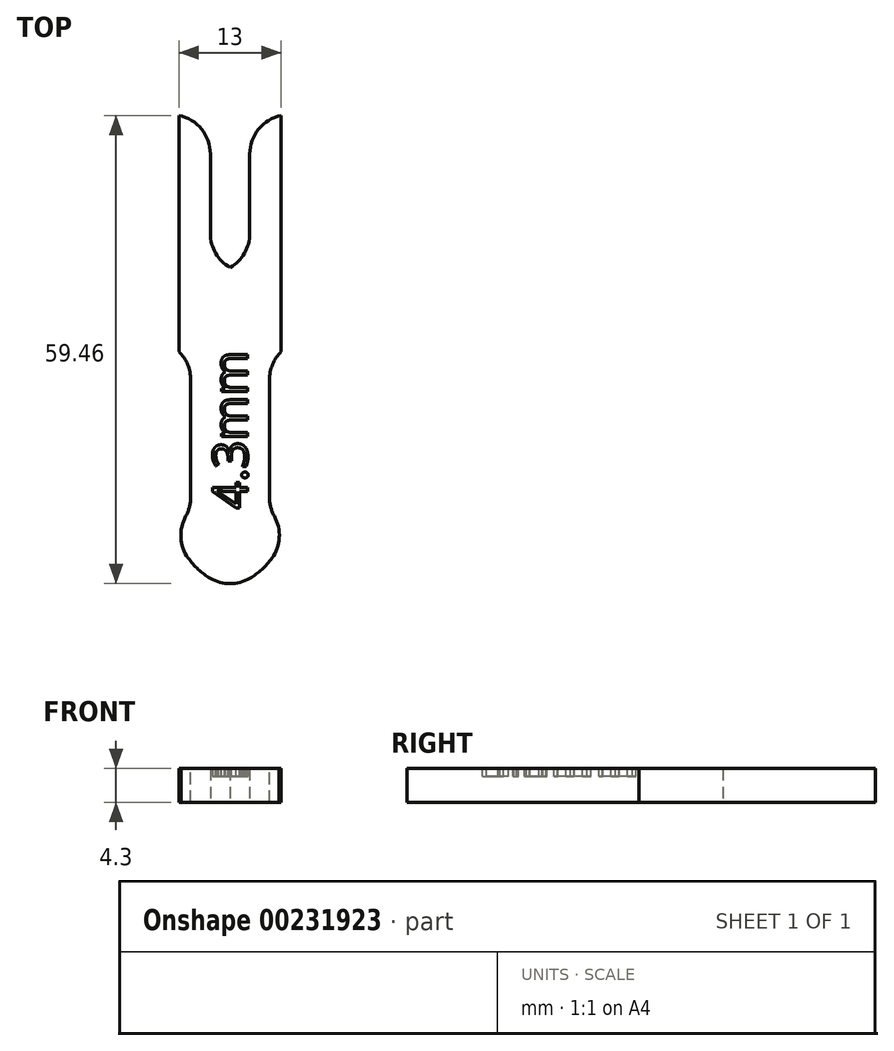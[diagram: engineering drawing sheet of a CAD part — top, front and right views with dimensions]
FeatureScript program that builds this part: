
annotation { "Feature Type Name" : "Feature", "Feature Type Description" : "" }
export const myFeature = defineFeature(function(context is Context, id is Id, definition is map)
    precondition{}
    {
        {
            var Q0;
            Q0=qCreatedBy(makeId("Top.planeOp"),FACE);
            var sketch = newSketch(context, id + "F0", { "sketchPlane" : qUnion([Q0])});
            skLineSegment(sketch, "E0", {"start": v(0, 0) * mm, "end": v(7, 0) * mm});
            skLineSegment(sketch, "E1", {"start": v(7, 0) * mm, "end": v(7, 10) * mm});
            skLineSegment(sketch, "E2", {"start": v(7, 10) * mm, "end": v(5, 10) * mm});
            skLineSegment(sketch, "E3", {"start": v(5, 10) * mm, "end": v(5, 30) * mm});
            skLineSegment(sketch, "E4", {"start": v(5, 30) * mm, "end": v(6.5, 30) * mm});
            skLineSegment(sketch, "E5", {"start": v(6.5, 30) * mm, "end": v(6.5, 60) * mm});
            skLineSegment(sketch, "E6", {"start": v(6.5, 60) * mm, "end": v(2.5, 60) * mm});
            skLineSegment(sketch, "E7", {"start": v(2.5, 60) * mm, "end": v(2.5, 40) * mm});
            skLineSegment(sketch, "E8", {"start": v(2.5, 40) * mm, "end": v(0, 40) * mm});
            skLineSegment(sketch, "E9.MirrorCS", {"start": v(-7, 10) * mm, "end": v(-5, 10) * mm});
            skLineSegment(sketch, "E10.MirrorCS", {"start": v(-5, 30) * mm, "end": v(-6.5, 30) * mm});
            skLineSegment(sketch, "E11.MirrorCS", {"start": v(-5, 10) * mm, "end": v(-5, 30) * mm});
            skLineSegment(sketch, "E12.MirrorCS", {"start": v(-2.5, 40) * mm, "end": v(0, 40) * mm});
            skLineSegment(sketch, "E13.MirrorCS", {"start": v(-6.5, 30) * mm, "end": v(-6.5, 60) * mm});
            skLineSegment(sketch, "E14.MirrorCS", {"start": v(0, 0) * mm, "end": v(-7, 0) * mm});
            skLineSegment(sketch, "E15.MirrorCS", {"start": v(-2.5, 60) * mm, "end": v(-2.5, 40) * mm});
            skLineSegment(sketch, "E16.MirrorCS", {"start": v(-6.5, 60) * mm, "end": v(-2.5, 60) * mm});
            skLineSegment(sketch, "E17.MirrorCS", {"start": v(-7, 0) * mm, "end": v(-7, 10) * mm});
            skSolve(sketch);
        }
        {
            var Q0;
            Q0 = qSketchRegion(id + "F0", true);
            extrude(context, id + "F1", {"entities" : qUnion([Q0]), "depth" : 4.3 * mm});
        }
        {
            var Q0;
            Q0=makeQuery(id+"F1.opExtrude","CAP_FACE",FACE,{"disambiguationData":[OSD([sQuery(id+"F0.wireOp",EDGE,"E0"),sQuery(id+"F0.wireOp",EDGE,"E1"),sQuery(id+"F0.wireOp",EDGE,"E2"),sQuery(id+"F0.wireOp",EDGE,"E3"),sQuery(id+"F0.wireOp",EDGE,"E4"),sQuery(id+"F0.wireOp",EDGE,"E5"),sQuery(id+"F0.wireOp",EDGE,"E6"),sQuery(id+"F0.wireOp",EDGE,"E7"),sQuery(id+"F0.wireOp",EDGE,"E8"),sQuery(id+"F0.wireOp",EDGE,"E9.MirrorCS"),sQuery(id+"F0.wireOp",EDGE,"E10.MirrorCS"),sQuery(id+"F0.wireOp",EDGE,"E11.MirrorCS"),sQuery(id+"F0.wireOp",EDGE,"E12.MirrorCS"),sQuery(id+"F0.wireOp",EDGE,"E13.MirrorCS"),sQuery(id+"F0.wireOp",EDGE,"E14.MirrorCS"),sQuery(id+"F0.wireOp",EDGE,"E15.MirrorCS"),sQuery(id+"F0.wireOp",EDGE,"E16.MirrorCS"),sQuery(id+"F0.wireOp",EDGE,"E17.MirrorCS")])],"isStart":false});
            var sketch = newSketch(context, id + "F2", { "sketchPlane" : qUnion([Q0])});
            skLineSegment(sketch, "E18", {"start": v(0, 10) * mm, "end": v(0, 30) * mm, "construction": true});
            skText(sketch, "E19", { "text": "4.3mm", "fontName": "OpenSans-Regular.ttf"});
            skPoint(sketch, "E20", {"position": v(0, 10) * mm});
            skPoint(sketch, "E21", {"position": v(0, 30) * mm});
            const initialGuessF2  = {"E19": [0.00221, 0.01, 0, 1, 0.00443]};
            skSetInitialGuess(sketch, initialGuessF2);
            skSolve(sketch);
        }
        {
            var Q0;
            Q0 = qSketchRegion(id + "F2", true);
            extrude(context, id + "F3", {"entities" : qUnion([Q0]), "operationType" : NewBodyOperationType.REMOVE, "oppositeDirection" : true, "depth" : 1 * mm});
        }
        {
            var Q0;
            Q0=makeQuery(id+"F1.opExtrude","SWEPT_EDGE",EDGE,{"disambiguationData":[OSD([sQuery(id+"F0.wireOp",EDGE,"E0"),sQuery(id+"F0.wireOp",EDGE,"E1")])]});
            var Q1;
            Q1=makeQuery(id+"F1.opExtrude","SWEPT_EDGE",EDGE,{"disambiguationData":[OSD([sQuery(id+"F0.wireOp",EDGE,"E1"),sQuery(id+"F0.wireOp",EDGE,"E2")])]});
            var Q2;
            Q2=makeQuery(id+"F1.opExtrude","SWEPT_EDGE",EDGE,{"disambiguationData":[OSD([sQuery(id+"F0.wireOp",EDGE,"E14.MirrorCS"),sQuery(id+"F0.wireOp",EDGE,"E17.MirrorCS")])]});
            var Q3;
            Q3=makeQuery(id+"F1.opExtrude","SWEPT_EDGE",EDGE,{"disambiguationData":[OSD([sQuery(id+"F0.wireOp",EDGE,"E9.MirrorCS"),sQuery(id+"F0.wireOp",EDGE,"E17.MirrorCS")])]});
            fillet(context, id + "F4", {"entities" : qUnion([Q0, Q1, Q2, Q3]), "radius" : 9 * mm, "tangentPropagation" : true, "allowEdgeOverflow" : false});
        }
        {
            var Q0;
            Q0=makeQuery(id+"F4.opFillet","BLEND_EDGE",EDGE,{"blendedFrom":[makeQuery(id+"F1.opExtrude","SWEPT_EDGE",EDGE,{"disambiguationData":[OSD([sQuery(id+"F0.wireOp",EDGE,"E0"),sQuery(id+"F0.wireOp",EDGE,"E1")])]}),makeQuery(id+"F1.opExtrude","SWEPT_EDGE",EDGE,{"disambiguationData":[OSD([sQuery(id+"F0.wireOp",EDGE,"E14.MirrorCS"),sQuery(id+"F0.wireOp",EDGE,"E17.MirrorCS")])]})],"blendedInto":[]});
            var Q1;
            {var subQ0=sQuery(id+"F0.wireOp",EDGE,"E1");Q1=makeQuery(id+"F4.opFillet","BLEND_EDGE",EDGE,{"blendedFrom":[makeQuery(id+"F1.opExtrude","SWEPT_EDGE",EDGE,{"disambiguationData":[OSD([sQuery(id+"F0.wireOp",EDGE,"E0"),subQ0])]}),makeQuery(id+"F1.opExtrude","SWEPT_EDGE",EDGE,{"disambiguationData":[OSD([subQ0,sQuery(id+"F0.wireOp",EDGE,"E2")])]})],"blendedInto":[]});}
            var Q2;
            {var subQ0=sQuery(id+"F0.wireOp",EDGE,"E17.MirrorCS");Q2=makeQuery(id+"F4.opFillet","BLEND_EDGE",EDGE,{"blendedFrom":[makeQuery(id+"F1.opExtrude","SWEPT_EDGE",EDGE,{"disambiguationData":[OSD([sQuery(id+"F0.wireOp",EDGE,"E9.MirrorCS"),subQ0])]}),makeQuery(id+"F1.opExtrude","SWEPT_EDGE",EDGE,{"disambiguationData":[OSD([sQuery(id+"F0.wireOp",EDGE,"E14.MirrorCS"),subQ0])]})],"blendedInto":[]});}
            fillet(context, id + "F5", {"entities" : qUnion([Q0, Q1, Q2]), "radius" : 5 * mm, "tangentPropagation" : true, "allowEdgeOverflow" : false});
        }
        {
            var Q0;
            Q0=makeQuery(id+"F4.opFillet","BLEND_EDGE",EDGE,{"blendedFrom":[makeQuery(id+"F1.opExtrude","SWEPT_EDGE",EDGE,{"disambiguationData":[OSD([sQuery(id+"F0.wireOp",EDGE,"E1"),sQuery(id+"F0.wireOp",EDGE,"E2")])]}),makeQuery(id+"F1.opExtrude","SWEPT_FACE",FACE,{"disambiguationData":[OSD([sQuery(id+"F0.wireOp",EDGE,"E3")])]})],"blendedInto":[makeQuery(id+"F1.opExtrude","SWEPT_FACE",FACE,{"disambiguationData":[OSD([sQuery(id+"F0.wireOp",EDGE,"E3")])]})]});
            var Q1;
            Q1=makeQuery(id+"F4.opFillet","BLEND_EDGE",EDGE,{"blendedFrom":[makeQuery(id+"F1.opExtrude","SWEPT_EDGE",EDGE,{"disambiguationData":[OSD([sQuery(id+"F0.wireOp",EDGE,"E9.MirrorCS"),sQuery(id+"F0.wireOp",EDGE,"E17.MirrorCS")])]}),makeQuery(id+"F1.opExtrude","SWEPT_FACE",FACE,{"disambiguationData":[OSD([sQuery(id+"F0.wireOp",EDGE,"E11.MirrorCS")])]})],"blendedInto":[makeQuery(id+"F1.opExtrude","SWEPT_FACE",FACE,{"disambiguationData":[OSD([sQuery(id+"F0.wireOp",EDGE,"E11.MirrorCS")])]})]});
            var Q2;
            Q2=makeQuery(id+"F1.opExtrude","SWEPT_EDGE",EDGE,{"disambiguationData":[OSD([sQuery(id+"F0.wireOp",EDGE,"E10.MirrorCS"),sQuery(id+"F0.wireOp",EDGE,"E11.MirrorCS")])]});
            var Q3;
            Q3=makeQuery(id+"F1.opExtrude","SWEPT_EDGE",EDGE,{"disambiguationData":[OSD([sQuery(id+"F0.wireOp",EDGE,"E3"),sQuery(id+"F0.wireOp",EDGE,"E4")])]});
            fillet(context, id + "F6", {"entities" : qUnion([Q0, Q1, Q2, Q3]), "radius" : 5 * mm, "tangentPropagation" : true, "allowEdgeOverflow" : false});
        }
        {
            var Q0;
            Q0=makeQuery(id+"F1.opExtrude","SWEPT_EDGE",EDGE,{"disambiguationData":[OSD([sQuery(id+"F0.wireOp",EDGE,"E15.MirrorCS"),sQuery(id+"F0.wireOp",EDGE,"E16.MirrorCS")])]});
            var Q1;
            Q1=makeQuery(id+"F1.opExtrude","SWEPT_EDGE",EDGE,{"disambiguationData":[OSD([sQuery(id+"F0.wireOp",EDGE,"E6"),sQuery(id+"F0.wireOp",EDGE,"E7")])]});
            fillet(context, id + "F7", {"entities" : qUnion([Q0, Q1]), "radius" : 5 * mm, "tangentPropagation" : true, "allowEdgeOverflow" : false});
        }
        {
            var Q0;
            Q0=makeQuery(id+"F1.opExtrude","SWEPT_EDGE",EDGE,{"disambiguationData":[OSD([sQuery(id+"F0.wireOp",EDGE,"E12.MirrorCS"),sQuery(id+"F0.wireOp",EDGE,"E15.MirrorCS")])]});
            var Q1;
            Q1=makeQuery(id+"F1.opExtrude","SWEPT_EDGE",EDGE,{"disambiguationData":[OSD([sQuery(id+"F0.wireOp",EDGE,"E7"),sQuery(id+"F0.wireOp",EDGE,"E8")])]});
            fillet(context, id + "F8", {"entities" : qUnion([Q0, Q1]), "radius" : 5 * mm, "tangentPropagation" : true, "allowEdgeOverflow" : false});
        }
    });
